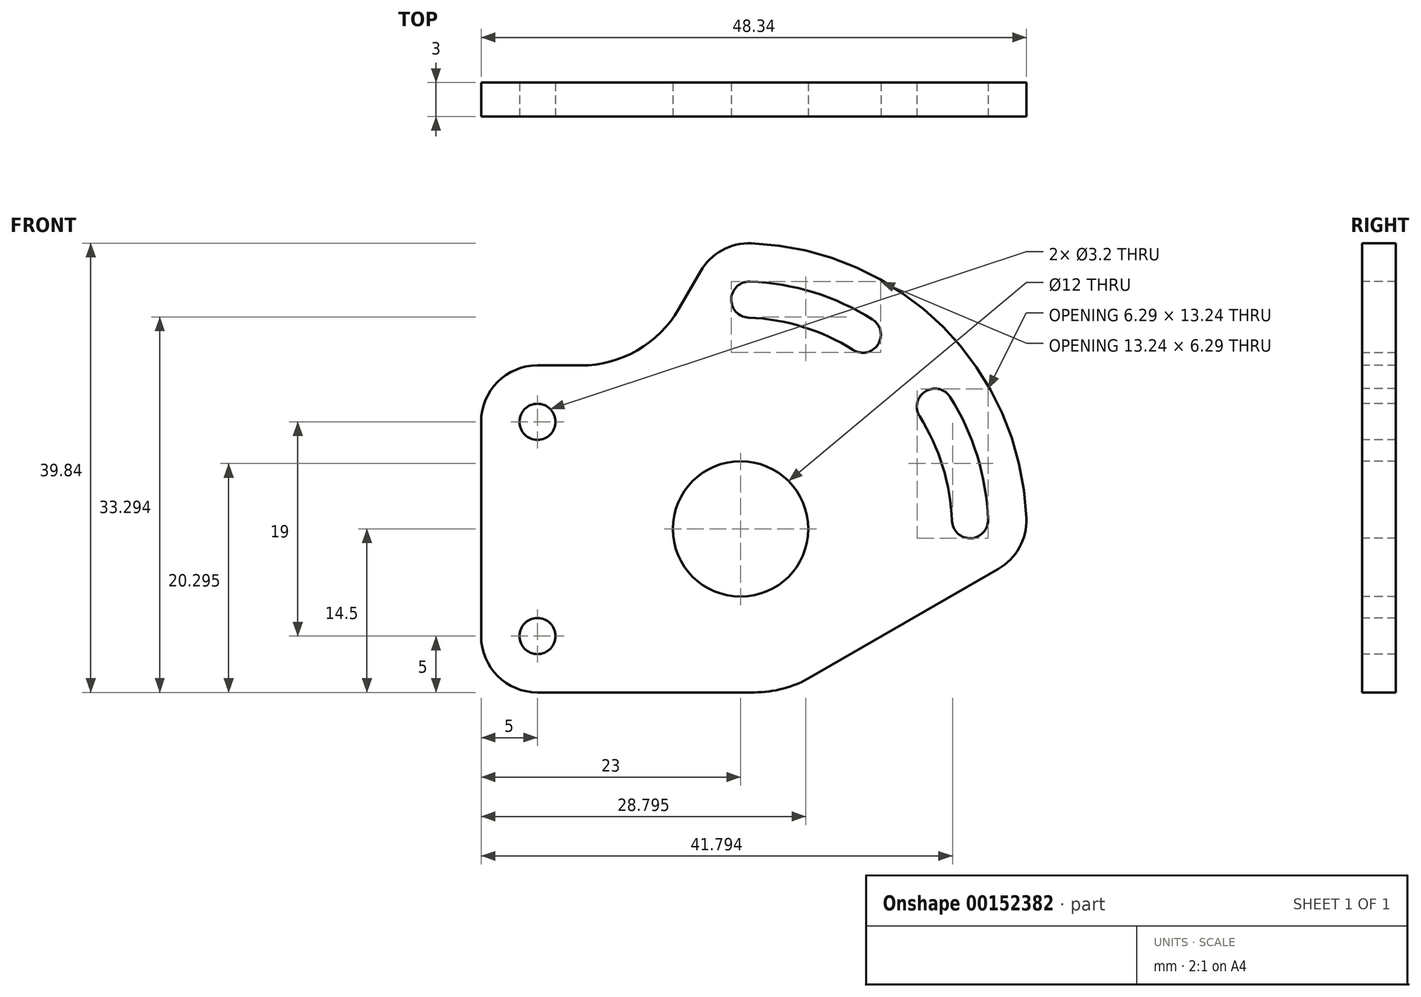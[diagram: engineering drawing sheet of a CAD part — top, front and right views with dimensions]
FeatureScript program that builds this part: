
annotation { "Feature Type Name" : "Feature", "Feature Type Description" : "" }
export const myFeature = defineFeature(function(context is Context, id is Id, definition is map)
    precondition{}
    {
        {
            var Q0;
            Q0=qCreatedBy(makeId("Front.planeOp"),FACE);
            var sketch = newSketch(context, id + "F0", { "sketchPlane" : qUnion([Q0])});
            skLineSegment(sketch, "E0.bottom", {"start": v(-18, 14.5) * mm, "end": v(-14.15, 14.5) * mm});
            skLineSegment(sketch, "E0.top", {"start": v(-18, -14.5) * mm, "end": v(1.2, -14.5) * mm});
            skLineSegment(sketch, "E0.left", {"start": v(-23, 9.5) * mm, "end": v(-23, -9.5) * mm});
            skPoint(sketch, "E1", {"position": v(0, 0) * mm});
            skPoint(sketch, "E2", {"position": v(-18, 9.5) * mm});
            skPoint(sketch, "E3", {"position": v(-18, -9.5) * mm});
            skArc(sketch, "E4", {"start": v(20.34, 0.77) * mm, "mid": v(19.45, 6.01) * mm, "end": v(17.23, 10.84) * mm, "construction": true});
            skLineSegment(sketch, "E5", {"start": v(0, 0) * mm, "end": v(38.42, 22.18) * mm, "construction": true});
            skLineSegment(sketch, "E6", {"start": v(0, 0) * mm, "end": v(75.1, 0) * mm});
            skLineSegment(sketch, "E7", {"start": v(0, 0) * mm, "end": v(21.8, 37.77) * mm, "construction": true});
            skCircle(sketch, "E8", {"center": v(15.59, 9) * mm, "radius": 9.5 * mm, "construction": true});
            skPoint(sketch, "E9", {"position": v(10.84, 17.23) * mm});
            skPoint(sketch, "E10", {"position": v(20.34, 0.77) * mm});
            skCircle(sketch, "E11", {"center": v(9, 15.59) * mm, "radius": 9.5 * mm, "construction": true});
            skPoint(sketch, "E12", {"position": v(0.77, 20.34) * mm});
            skPoint(sketch, "E13", {"position": v(17.23, 10.84) * mm});
            skLineSegment(sketch, "E14", {"start": v(0.77, 20.34) * mm, "end": v(-3.56, 22.84) * mm, "construction": true});
            skLineSegment(sketch, "E15", {"start": v(-3.56, 22.84) * mm, "end": v(-5.48, 19.5) * mm});
            skLineSegment(sketch, "E16.trimOffspring", {"start": v(7.84, 14.5) * mm, "end": v(8.37, 14.5) * mm});
            skLineSegment(sketch, "E17", {"start": v(20.34, 0.77) * mm, "end": v(22.84, -3.56) * mm, "construction": true});
            skLineSegment(sketch, "E18", {"start": v(22.84, -3.56) * mm, "end": v(6.2, -13.16) * mm});
            skArc(sketch, "E19", {"start": v(0.96, 25.33) * mm, "mid": v(17.93, 17.93) * mm, "end": v(25.33, 0.96) * mm});
            skPoint(sketch, "E20.visualSharp", {"position": v(-23, 14.5) * mm});
            skArc(sketch, "E20.filletArc", {"start": v(-18, 14.5) * mm, "mid": v(-21.54, 13.04) * mm, "end": v(-23, 9.5) * mm});
            skPoint(sketch, "E21.visualSharp", {"position": v(-23, -14.5) * mm});
            skArc(sketch, "E21.filletArc", {"start": v(-23, -9.5) * mm, "mid": v(-21.54, -13.04) * mm, "end": v(-18, -14.5) * mm});
            skPoint(sketch, "E22.visualSharp", {"position": v(-2.16, 25.26) * mm});
            skArc(sketch, "E22.filletArc", {"start": v(0.96, 25.33) * mm, "mid": v(-1.64, 24.72) * mm, "end": v(-3.56, 22.84) * mm});
            skPoint(sketch, "E23.visualSharp", {"position": v(25.26, -2.16) * mm});
            skArc(sketch, "E23.filletArc", {"start": v(22.84, -3.56) * mm, "mid": v(24.72, -1.64) * mm, "end": v(25.33, 0.96) * mm});
            skPoint(sketch, "E24.visualSharp", {"position": v(-8.37, 14.5) * mm});
            skArc(sketch, "E24.filletArc", {"start": v(-14.15, 14.5) * mm, "mid": v(-9.15, 15.84) * mm, "end": v(-5.48, 19.5) * mm});
            skPoint(sketch, "E25.visualSharp", {"position": v(3.89, -14.5) * mm});
            skArc(sketch, "E25.filletArc", {"start": v(1.2, -14.5) * mm, "mid": v(3.8, -14.16) * mm, "end": v(6.2, -13.16) * mm});
            skArc(sketch, "E26.trimOffspring", {"start": v(-5.42, 19.62) * mm, "mid": v(-14.4, -14.4) * mm, "end": v(19.62, -5.42) * mm, "construction": true});
            skArc(sketch, "E27.trimOffspring", {"start": v(10.84, 17.23) * mm, "mid": v(6.01, 19.45) * mm, "end": v(0.77, 20.34) * mm, "construction": true});
            skArc(sketch, "E28.0.startCap", {"start": v(11.7, 18.58) * mm, "mid": v(12.2, 16.38) * mm, "end": v(9.99, 15.87) * mm});
            skArc(sketch, "E28.0.endCap", {"start": v(0.71, 18.74) * mm, "mid": v(-0.83, 20.4) * mm, "end": v(0.83, 21.94) * mm});
            skArc(sketch, "E28.0.left", {"start": v(9.99, 15.87) * mm, "mid": v(5.54, 17.92) * mm, "end": v(0.71, 18.74) * mm});
            skArc(sketch, "E28.0.right", {"start": v(11.7, 18.58) * mm, "mid": v(6.48, 20.97) * mm, "end": v(0.83, 21.94) * mm});
            skArc(sketch, "E29.0.startCap", {"start": v(21.94, 0.83) * mm, "mid": v(20.4, -0.83) * mm, "end": v(18.74, 0.71) * mm});
            skArc(sketch, "E29.0.endCap", {"start": v(15.87, 9.99) * mm, "mid": v(16.38, 12.2) * mm, "end": v(18.58, 11.7) * mm});
            skArc(sketch, "E29.0.left", {"start": v(18.74, 0.71) * mm, "mid": v(17.92, 5.54) * mm, "end": v(15.87, 9.99) * mm});
            skArc(sketch, "E29.0.right", {"start": v(21.94, 0.83) * mm, "mid": v(20.97, 6.48) * mm, "end": v(18.58, 11.7) * mm});
            skCircle(sketch, "E30", {"center": v(-18, 9.5) * mm, "radius": 1.6 * mm});
            skCircle(sketch, "E31", {"center": v(-18, -9.5) * mm, "radius": 1.6 * mm});
            skCircle(sketch, "E32", {"center": v(0, 0) * mm, "radius": 6 * mm});
            skSolve(sketch);
        }
        {
            var Q0;
            Q0=makeQuery(id+"F0.imprint","IMPRINT",FACE,{"disambiguationData":[TD([[makeQuery(id+"F0.imprint","IMPRINT",EDGE,{"derivedFrom":sQuery(id+"F0.wireOp",EDGE,"E0.bottom")}),-1.0]])]});
            extrude(context, id + "F1", {"entities" : qUnion([Q0]), "oppositeDirection" : true, "depth" : 3 * mm});
        }
    });
